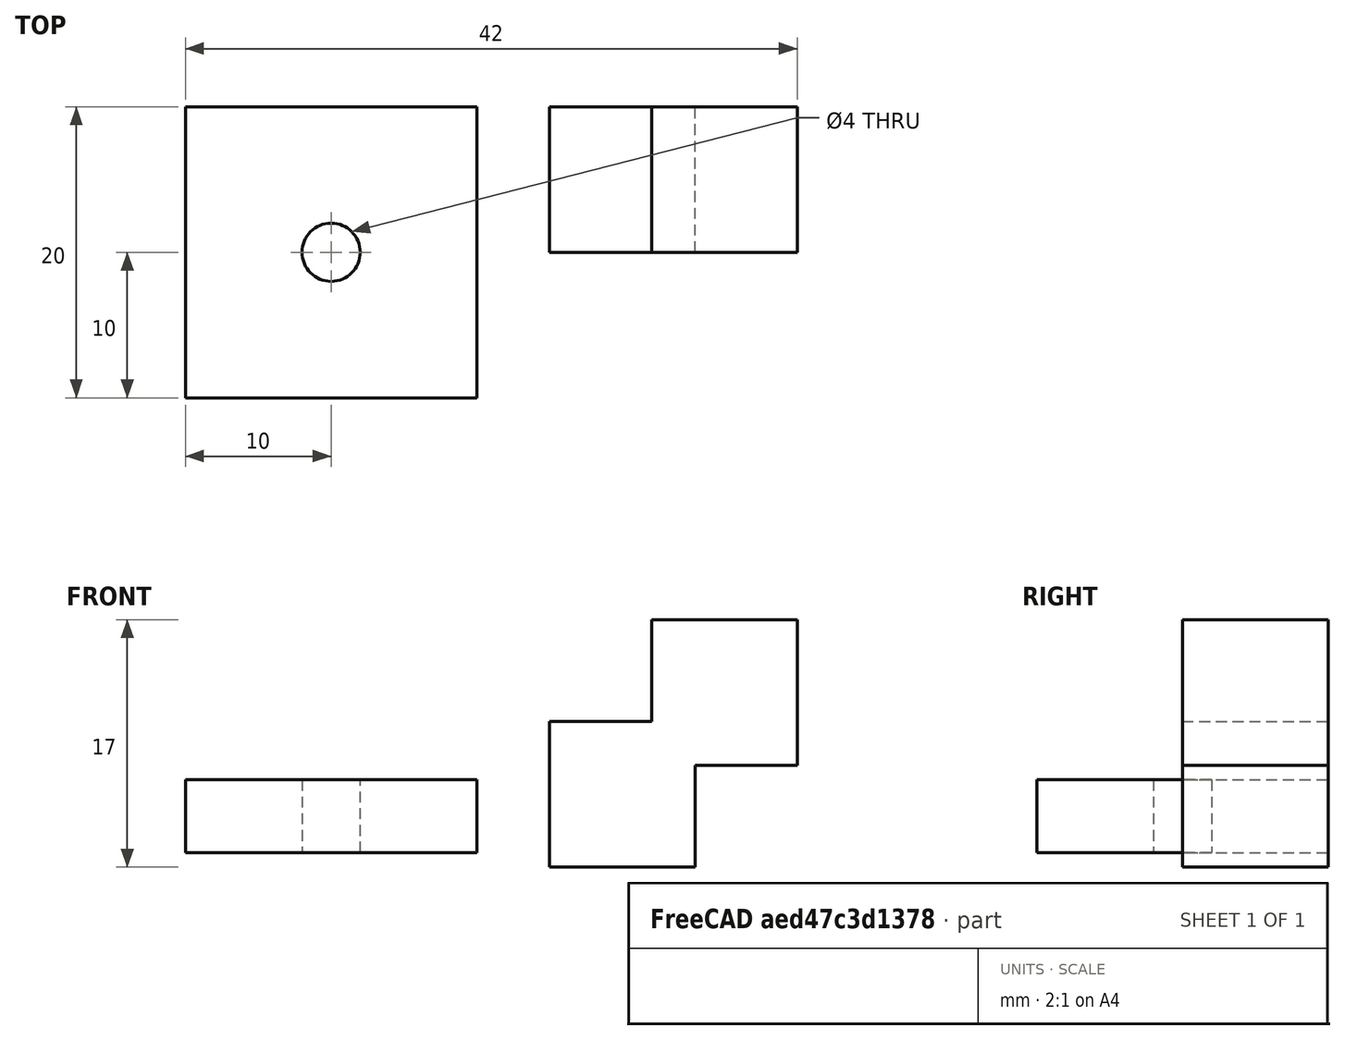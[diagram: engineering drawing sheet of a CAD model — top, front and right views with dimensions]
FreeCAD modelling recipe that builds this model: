
FCSTD DOCUMENT  (FreeCAD 0.20R29410 (Git))
Label: test
License: Creative Commons Attribution
LicenseURL: http://creativecommons.org/licenses/by/4.0/
objects: Part::Box×3, Part::Cylinder×1, Part::Cut×1, Part::MultiFuse×1
note: 6 computed .brp shape members not serialized (recipe doc carries the construction recipe); baked Part::Feature solids carry a one-line shape summary decoded from their .brp

FEATURE [Part::Box] Box  label="Cube"
  AttacherType = Attacher::AttachEngine3D
  Height = 5
  Length = 20
  Placement = pos=(-10,-10,1) rot=(0,0,1;0rad)
  Width = 20
FEATURE [Part::Cylinder] Cylinder
  Angle = 360
  AttacherType = Attacher::AttachEngine3D
  FirstAngle = 0
  Height = 10
  Radius = 2
  SecondAngle = 0
FEATURE [Part::Cut] Cut
  Base = -> Box
  Refine = true
  Tool = -> Cylinder
FEATURE [Part::Box] Box001  label="Cube001"
  AttacherType = Attacher::AttachEngine3D
  Height = 10
  Length = 10
  Placement = pos=(15,0,0) rot=(0,0,1;0rad)
  Width = 10
FEATURE [Part::Box] Box002  label="Cube002"
  AttacherType = Attacher::AttachEngine3D
  Height = 10
  Length = 10
  Placement = pos=(22,0,7) rot=(0,0,1;0rad)
  Width = 10
FEATURE [Part::MultiFuse] Fusion
  Refine = true
  Shapes = -> [Box002,Box001]
